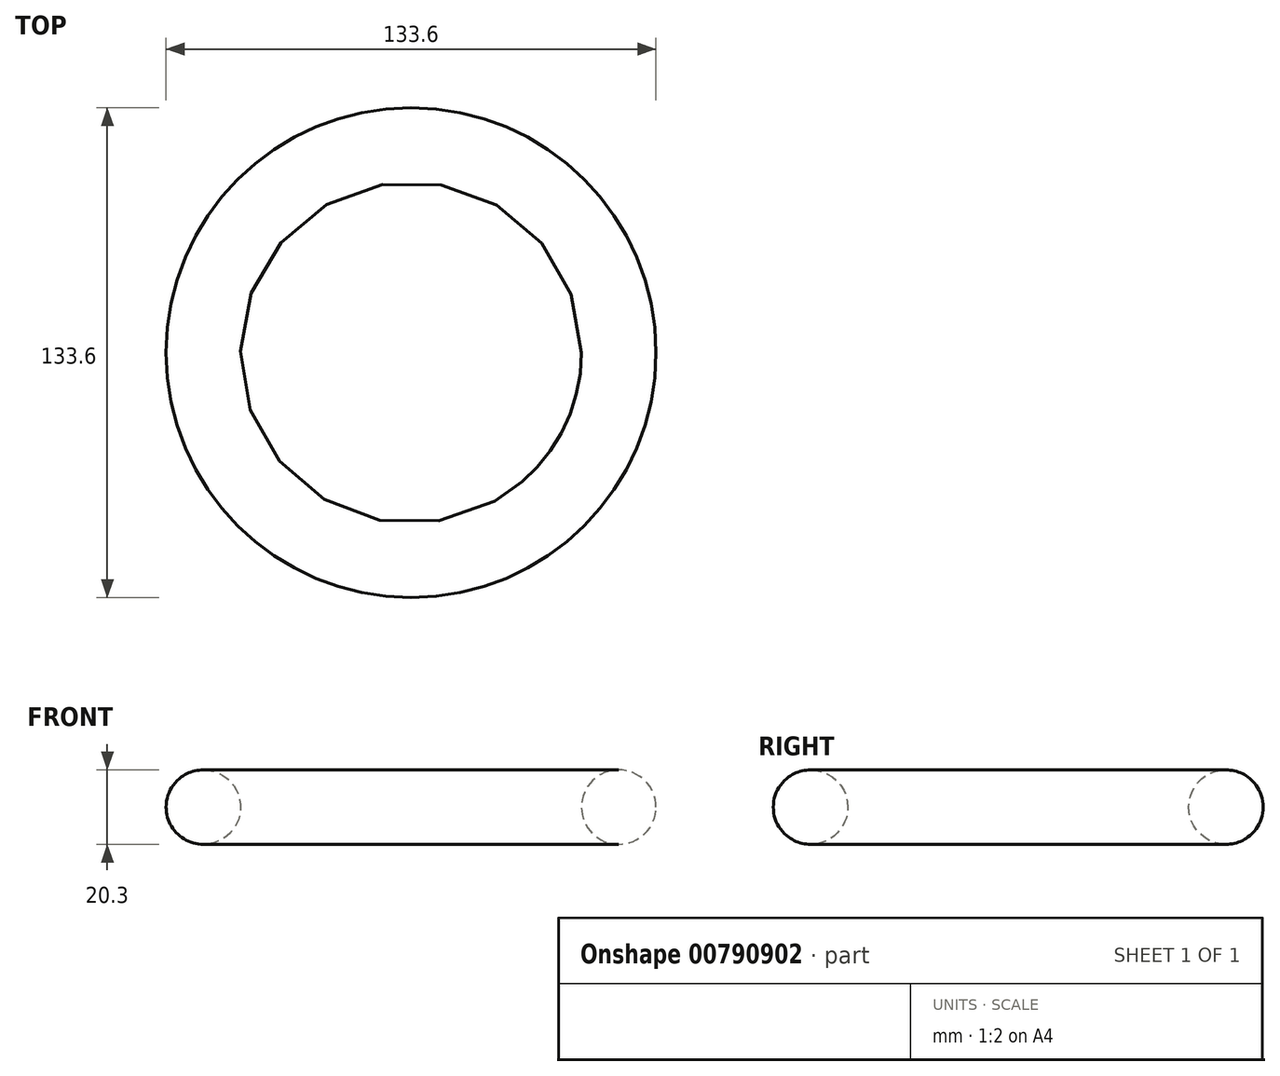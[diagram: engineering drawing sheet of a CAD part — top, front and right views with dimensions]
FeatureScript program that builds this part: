
annotation { "Feature Type Name" : "Feature", "Feature Type Description" : "" }
export const myFeature = defineFeature(function(context is Context, id is Id, definition is map)
    precondition{}
    {
        {
            var Q0;
            Q0=qCreatedBy(makeId("Front.planeOp"),FACE);
            var sketch = newSketch(context, id + "F0", { "sketchPlane" : qUnion([Q0])});
            skLineSegment(sketch, "E0", {"start": v(0, 41.96) * mm, "end": v(0, -10.4) * mm});
            skCircle(sketch, "E1", {"center": v(-56.64, 0) * mm, "radius": 10.15 * mm});
            skSolve(sketch);
        }
        {
            var Q0;
            Q0=makeQuery(id+"F0.imprint","IMPRINT",FACE,{"disambiguationData":[TD([[makeQuery(id+"F0.imprint","IMPRINT",EDGE,{"derivedFrom":sQuery(id+"F0.wireOp",EDGE,"E1")}),1.0]])]});
            var Q1;
            Q1=sQuery(id+"F0.wireOp",EDGE,"E0");
            revolve(context, id + "F1", {"surfaceOperationType" : NewSurfaceOperationType.NEW, "entities" : qUnion([Q0]), "axis" : qUnion([Q1]), "revolveType" : RevolveType.FULL});
        }
    });
